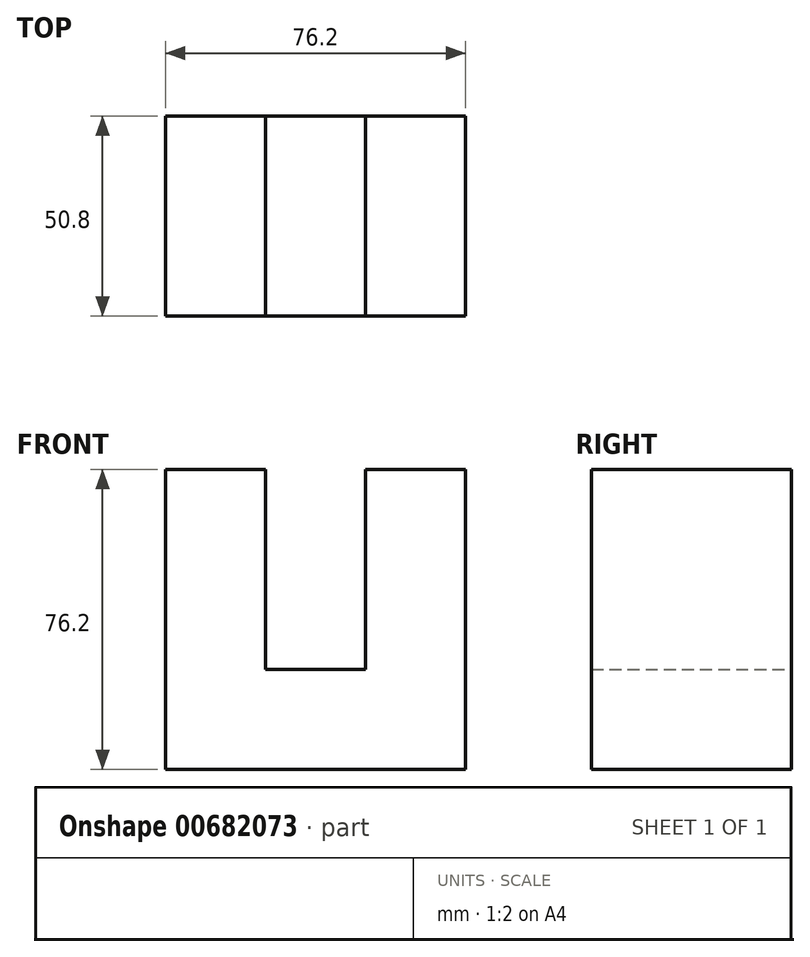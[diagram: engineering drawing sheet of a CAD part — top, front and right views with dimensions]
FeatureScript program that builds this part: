
annotation { "Feature Type Name" : "Feature", "Feature Type Description" : "" }
export const myFeature = defineFeature(function(context is Context, id is Id, definition is map)
    precondition{}
    {
        {
            var Q0;
            Q0=qCreatedBy(makeId("Front.planeOp"),FACE);
            var sketch = newSketch(context, id + "F0", { "sketchPlane" : qUnion([Q0])});
            skLineSegment(sketch, "E0", {"start": v(55.67, 0) * mm, "end": v(-20.53, 0) * mm});
            skLineSegment(sketch, "E1", {"start": v(-20.53, 0) * mm, "end": v(-20.53, 76.2) * mm});
            skLineSegment(sketch, "E2", {"start": v(-20.53, 76.2) * mm, "end": v(4.87, 76.2) * mm});
            skLineSegment(sketch, "E3", {"start": v(4.87, 76.2) * mm, "end": v(4.87, 25.4) * mm});
            skLineSegment(sketch, "E4", {"start": v(4.87, 25.4) * mm, "end": v(30.27, 25.4) * mm});
            skLineSegment(sketch, "E5", {"start": v(30.27, 25.4) * mm, "end": v(30.27, 76.2) * mm});
            skLineSegment(sketch, "E6", {"start": v(30.27, 76.2) * mm, "end": v(55.67, 76.2) * mm});
            skLineSegment(sketch, "E7", {"start": v(55.67, 76.2) * mm, "end": v(55.67, 0) * mm});
            skSolve(sketch);
        }
        {
            var Q0;
            Q0 = qSketchRegion(id + "F0", true);
            extrude(context, id + "F1", {"entities" : qUnion([Q0]), "depth" : 50.8 * mm, "offsetDistance" : 25.4 * mm});
        }
    });
